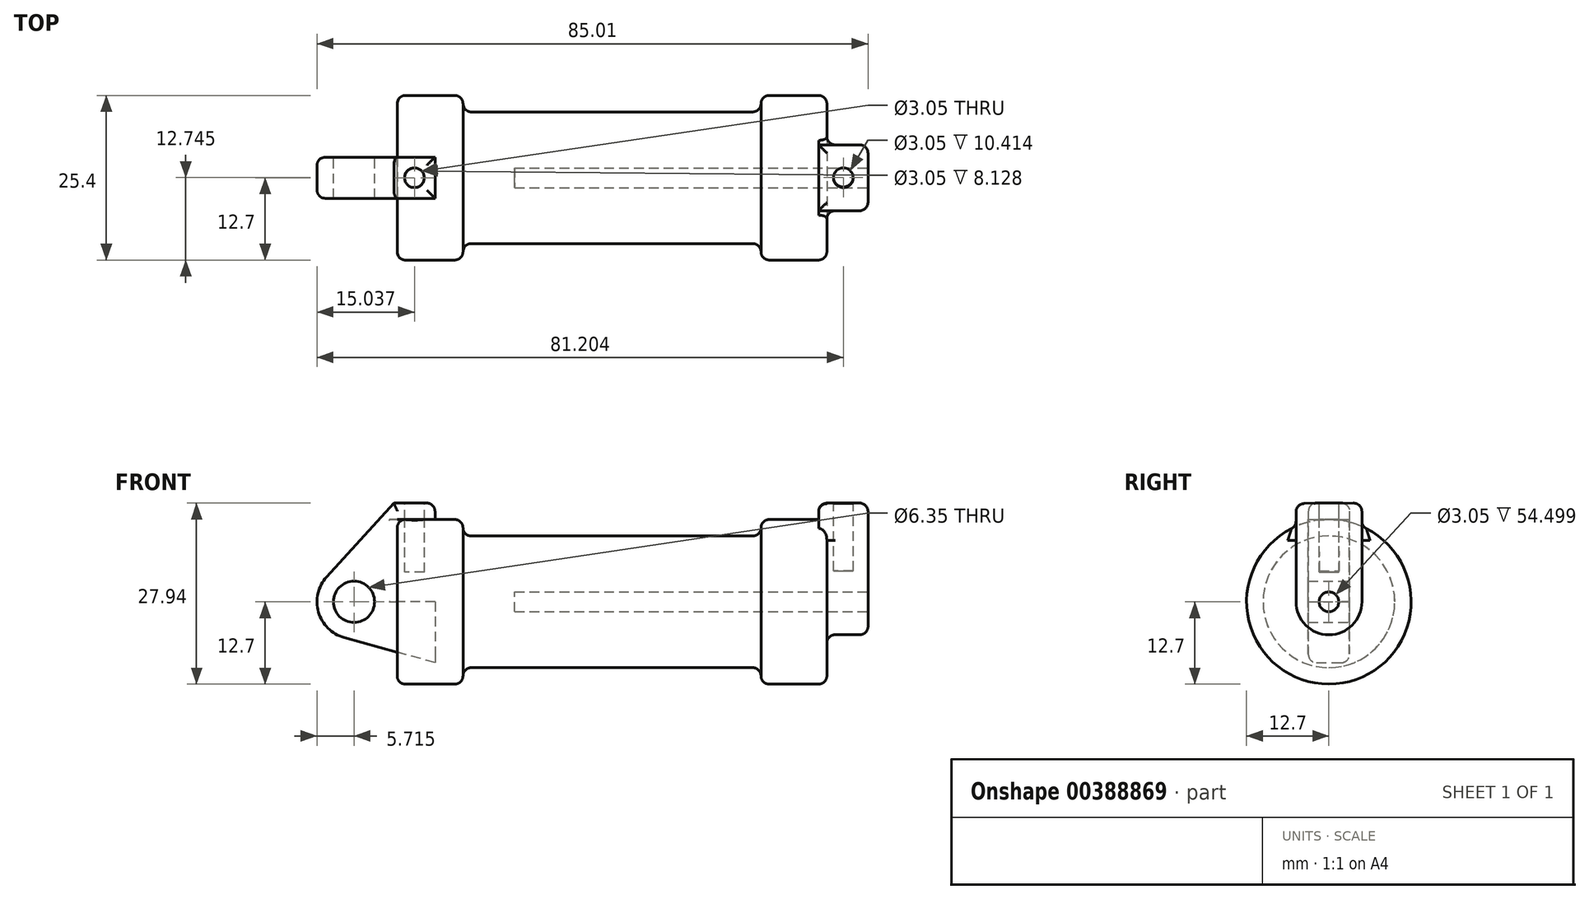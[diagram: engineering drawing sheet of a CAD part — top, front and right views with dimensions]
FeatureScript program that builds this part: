
annotation { "Feature Type Name" : "Feature", "Feature Type Description" : "" }
export const myFeature = defineFeature(function(context is Context, id is Id, definition is map)
    precondition{}
    {
        {
            var Q0;
            Q0=qCreatedBy(makeId("Front.planeOp"),FACE);
            var sketch = newSketch(context, id + "F0", { "sketchPlane" : qUnion([Q0])});
            skLineSegment(sketch, "E0", {"start": v(0, 0) * mm, "end": v(0, 12.7) * mm});
            skLineSegment(sketch, "E1", {"start": v(0, 12.7) * mm, "end": v(10.16, 12.7) * mm});
            skLineSegment(sketch, "E2", {"start": v(10.16, 12.7) * mm, "end": v(10.16, 10.16) * mm});
            skLineSegment(sketch, "E3", {"start": v(10.16, 10.16) * mm, "end": v(56.13, 10.16) * mm});
            skLineSegment(sketch, "E4", {"start": v(56.13, 10.16) * mm, "end": v(56.13, 12.7) * mm});
            skLineSegment(sketch, "E5", {"start": v(56.13, 12.7) * mm, "end": v(66.3, 12.7) * mm});
            skLineSegment(sketch, "E6", {"start": v(66.3, 12.7) * mm, "end": v(66.3, 0) * mm});
            skLineSegment(sketch, "E7", {"start": v(66.3, 0) * mm, "end": v(0, 0) * mm});
            skLineSegment(sketch, "E8", {"start": v(5.84, 15.24) * mm, "end": v(-0.5, 15.24) * mm});
            skLineSegment(sketch, "E9", {"start": v(-0.5, 15.24) * mm, "end": v(-10.88, 3.85) * mm});
            skLineSegment(sketch, "E10", {"start": v(0, 0) * mm, "end": v(-6.65, 0) * mm});
            skCircle(sketch, "E11", {"center": v(-6.65, 0) * mm, "radius": 5.72 * mm});
            skCircle(sketch, "E12", {"center": v(-6.65, 0) * mm, "radius": 3.18 * mm});
            skLineSegment(sketch, "E13", {"start": v(5.84, 15.24) * mm, "end": v(5.84, -9.4) * mm});
            skLineSegment(sketch, "E14", {"start": v(5.84, -9.4) * mm, "end": v(-8.18, -5.5) * mm});
            skSolve(sketch);
        }
        {
            var Q0;
            {var subQ0=sQuery(id+"F0.wireOp",EDGE,"E2");Q0=makeQuery(id+"F0.imprint","IMPRINT",FACE,{"disambiguationData":[TD([[makeQuery(id+"F0.imprint","IMPRINT",EDGE,{"derivedFrom":subQ0}),-1.0]])]});}
            var Q1;
            {var subQ0=sQuery(id+"F0.wireOp",EDGE,"E0");Q1=makeQuery(id+"F0.imprint","IMPRINT",FACE,{"disambiguationData":[TD([[makeQuery(id+"F0.imprint","IMPRINT",EDGE,{"derivedFrom":subQ0}),-1.0]])]});}
            var Q2;
            Q2=sQuery(id+"F0.wireOp",EDGE,"E7");
            revolve(context, id + "F1", {"entities" : qUnion([Q0, Q1]), "axis" : qUnion([Q2]), "revolveType" : RevolveType.FULL});
        }
        {
            var Q0;
            {var subQ5=sQuery(id+"F0.wireOp",EDGE,"E12");Q0=makeQuery(id+"F0.imprint","IMPRINT",FACE,{"disambiguationData":[TD([[makeQuery(id+"F0.imprint","IMPRINT",EDGE,{"derivedFrom":subQ5}),-1.0]])]});}
            var Q1;
            {var subQ0=sQuery(id+"F0.wireOp",EDGE,"E14");Q1=makeQuery(id+"F0.imprint","IMPRINT",FACE,{"disambiguationData":[TD([[makeQuery(id+"F0.imprint","IMPRINT",EDGE,{"derivedFrom":subQ0}),-1.0]])]});}
            var Q2;
            {var subQ1=sQuery(id+"F0.wireOp",EDGE,"E0");Q2=makeQuery(id+"F0.imprint","IMPRINT",FACE,{"disambiguationData":[TD([[makeQuery(id+"F0.imprint","IMPRINT",EDGE,{"derivedFrom":subQ1}),1.0]])]});}
            extrude(context, id + "F2", {"entities" : qUnion([Q0, Q1, Q2]), "endBound" : BoundingType.SYMMETRIC, "depth" : 6.35 * mm});
        }
        {
            var Q0;
            Q0=makeQuery(id+"F1.opRevolve","SWEPT_FACE",FACE,{"disambiguationData":[OSD([sQuery(id+"F0.wireOp",EDGE,"E6")])]});
            var sketch = newSketch(context, id + "F3", { "sketchPlane" : qUnion([Q0])});
            skCircle(sketch, "E15", {"center": v(0, 0) * mm, "radius": 1.52 * mm});
            skCircle(sketch, "E16", {"center": v(0, 0) * mm, "radius": 5.08 * mm});
            skLineSegment(sketch, "E17", {"start": v(5.08, 0) * mm, "end": v(5.08, 15.24) * mm});
            skLineSegment(sketch, "E18", {"start": v(-5.08, 0) * mm, "end": v(-5.08, 15.15) * mm});
            skLineSegment(sketch, "E19", {"start": v(-5.08, 15.15) * mm, "end": v(5.08, 15.24) * mm});
            skSolve(sketch);
        }
        {
            var Q0;
            {var subQ0=sQuery(id+"F3.wireOp",EDGE,"E17");var subQ1=sQuery(id+"F3.wireOp",EDGE,"E16");var subQ2=makeQuery(id+"F3.imprint","INTERSECT",VERTEX,{"derivedFrom":[subQ1,subQ0]});Q0=makeQuery(id+"F3.imprint","IMPRINT",FACE,{"disambiguationData":[TD([[makeQuery(id+"F3.imprint","IMPRINT",EDGE,{"disambiguationData":[TD([[subQ2,-1.0]])],"derivedFrom":subQ1}),-1.0]])]});}
            var Q1;
            Q1=makeQuery(id+"F3.imprint","IMPRINT",FACE,{"disambiguationData":[TD([[makeQuery(id+"F3.imprint","IMPRINT",EDGE,{"derivedFrom":sQuery(id+"F3.wireOp",EDGE,"E15")}),-1.0]])]});
            var Q2;
            {var subQ0=sQuery(id+"F3.wireOp",EDGE,"E19");Q2=makeQuery(id+"F3.imprint","IMPRINT",FACE,{"disambiguationData":[TD([[makeQuery(id+"F3.imprint","IMPRINT",EDGE,{"derivedFrom":subQ0}),-1.0]])]});}
            var Q3;
            Q3=makeQuery(id+"F3.imprint","IMPRINT",FACE,{"disambiguationData":[TD([[makeQuery(id+"F3.imprint","IMPRINT",EDGE,{"derivedFrom":sQuery(id+"F3.wireOp",EDGE,"E15")}),1.0]])]});
            extrude(context, id + "F4", {"entities" : qUnion([Q0, Q1, Q2, Q3]), "operationType" : NewBodyOperationType.ADD, "depth" : 6.35 * mm, "hasSecondDirection" : true, "secondDirectionOppositeDirection" : true, "secondDirectionDepth" : 1.27 * mm});
        }
        {
            var Q0;
            Q0=makeQuery(id+"F3.imprint","IMPRINT",FACE,{"disambiguationData":[TD([[makeQuery(id+"F3.imprint","IMPRINT",EDGE,{"derivedFrom":sQuery(id+"F3.wireOp",EDGE,"E15")}),1.0]])]});
            extrude(context, id + "F5", {"entities" : qUnion([Q0]), "operationType" : NewBodyOperationType.REMOVE, "oppositeDirection" : true, "depth" : 48.15 * mm, "hasSecondDirection" : true, "secondDirectionOppositeDirection" : false, "secondDirectionDepth" : 6.35 * mm});
        }
        {
            var Q0;
            Q0=makeQuery(id+"F4.opExtrude","SWEPT_FACE",FACE,{"disambiguationData":[OSD([sQuery(id+"F3.wireOp",EDGE,"E19")])]});
            var sketch = newSketch(context, id + "F6", { "sketchPlane" : qUnion([Q0])});
            skLineSegment(sketch, "E20", {"start": v(65.02, 0.13) * mm, "end": v(72.64, 0.13) * mm, "construction": true});
            skLineSegment(sketch, "E21", {"start": v(68.83, 5.21) * mm, "end": v(68.83, -4.95) * mm, "construction": true});
            skCircle(sketch, "E22", {"center": v(68.83, 0.13) * mm, "radius": 1.52 * mm});
            skSolve(sketch);
        }
        {
            var Q0;
            Q0=makeQuery(id+"F6.imprint","IMPRINT",FACE,{"disambiguationData":[TD([[makeQuery(id+"F6.imprint","IMPRINT",EDGE,{"derivedFrom":sQuery(id+"F6.wireOp",EDGE,"E22")}),1.0]])]});
            var Q1;
            Q1=sQuery(id+"F6.wireOp",EDGE,"E22");
            extrude(context, id + "F7", {"entities" : qUnion([Q0]), "operationType" : NewBodyOperationType.REMOVE, "surfaceEntities" : qUnion([Q1]), "oppositeDirection" : true, "depth" : 10.4 * mm});
        }
        {
            var Q0;
            Q0=makeQuery(id+"F2.opExtrude","SWEPT_FACE",FACE,{"disambiguationData":[OSD([sQuery(id+"F0.wireOp",EDGE,"E8")])]});
            var sketch = newSketch(context, id + "F8", { "sketchPlane" : qUnion([Q0])});
            skLineSegment(sketch, "E23.0", {"start": v(5.84, 3.18) * mm, "end": v(-0.5, 3.18) * mm});
            skLineSegment(sketch, "E23.1", {"start": v(5.84, -3.18) * mm, "end": v(5.84, 3.17) * mm});
            skLineSegment(sketch, "E23.2", {"start": v(5.84, -3.18) * mm, "end": v(-0.5, -3.18) * mm});
            skLineSegment(sketch, "E23.3", {"start": v(-0.5, -3.18) * mm, "end": v(-0.5, 3.17) * mm});
            skLineSegment(sketch, "E24", {"start": v(2.67, 3.18) * mm, "end": v(2.67, -3.18) * mm, "construction": true});
            skLineSegment(sketch, "E25", {"start": v(-0.5, 0) * mm, "end": v(5.84, 0) * mm, "construction": true});
            skCircle(sketch, "E26", {"center": v(2.67, 0) * mm, "radius": 1.52 * mm});
            skSolve(sketch);
        }
        {
            var Q0;
            Q0=makeQuery(id+"F8.imprint","IMPRINT",FACE,{"disambiguationData":[TD([[makeQuery(id+"F8.imprint","IMPRINT",EDGE,{"derivedFrom":sQuery(id+"F8.wireOp",EDGE,"E26")}),1.0]])]});
            var Q1;
            Q1=sQuery(id+"F8.wireOp",EDGE,"E26");
            extrude(context, id + "F9", {"entities" : qUnion([Q0]), "operationType" : NewBodyOperationType.REMOVE, "surfaceEntities" : qUnion([Q1]), "oppositeDirection" : true, "depth" : 10.67 * mm});
        }
        {
            var Q0;
            Q0=makeQuery(id+"F1.opRevolve","SWEPT_EDGE",EDGE,{"disambiguationData":[OSD([sQuery(id+"F0.wireOp",EDGE,"E0"),sQuery(id+"F0.wireOp",EDGE,"E1")])]});
            var Q1;
            Q1=makeQuery(id+"F1.opRevolve","SWEPT_EDGE",EDGE,{"disambiguationData":[OSD([sQuery(id+"F0.wireOp",EDGE,"E1"),sQuery(id+"F0.wireOp",EDGE,"E2")])]});
            var Q2;
            Q2=makeQuery(id+"F1.opRevolve","SWEPT_EDGE",EDGE,{"disambiguationData":[OSD([sQuery(id+"F0.wireOp",EDGE,"E4"),sQuery(id+"F0.wireOp",EDGE,"E5")])]});
            var Q3;
            Q3=makeQuery(id+"F1.opRevolve","SWEPT_EDGE",EDGE,{"disambiguationData":[OSD([sQuery(id+"F0.wireOp",EDGE,"E5"),sQuery(id+"F0.wireOp",EDGE,"E6")])]});
            var Q4;
            Q4=makeQuery(id+"F1.opRevolve","SWEPT_EDGE",EDGE,{"disambiguationData":[OSD([sQuery(id+"F0.wireOp",EDGE,"E2"),sQuery(id+"F0.wireOp",EDGE,"E3")])]});
            var Q5;
            Q5=makeQuery(id+"F1.opRevolve","SWEPT_EDGE",EDGE,{"disambiguationData":[OSD([sQuery(id+"F0.wireOp",EDGE,"E3"),sQuery(id+"F0.wireOp",EDGE,"E4")])]});
            fillet(context, id + "F10", {"entities" : qUnion([Q0, Q1, Q2, Q3, Q4, Q5]), "radius" : 1.27 * mm, "tangentPropagation" : true, "allowEdgeOverflow" : false});
        }
        {
            var Q0;
            Q0=makeQuery(id+"F2.opExtrude","CAP_EDGE",EDGE,{"disambiguationData":[OSD([sQuery(id+"F0.wireOp",EDGE,"E9")])],"isStart":true});
            var Q1;
            Q1=makeQuery(id+"F2.opExtrude","CAP_EDGE",EDGE,{"disambiguationData":[OSD([sQuery(id+"F0.wireOp",EDGE,"E8")])],"isStart":true});
            var Q2;
            Q2=makeQuery(id+"F2.opExtrude","SWEPT_EDGE",EDGE,{"disambiguationData":[OSD([sQuery(id+"F0.wireOp",EDGE,"E8"),sQuery(id+"F0.wireOp",EDGE,"E13")])]});
            var Q3;
            Q3=makeQuery(id+"F2.opExtrude","CAP_EDGE",EDGE,{"disambiguationData":[OSD([sQuery(id+"F0.wireOp",EDGE,"E8")])],"isStart":false});
            var Q4;
            Q4=makeQuery(id+"F2.opExtrude","CAP_EDGE",EDGE,{"disambiguationData":[OSD([sQuery(id+"F0.wireOp",EDGE,"E9")])],"isStart":false});
            var Q5;
            Q5=makeQuery(id+"F2.opExtrude","CAP_EDGE",EDGE,{"disambiguationData":[OSD([sQuery(id+"F0.wireOp",EDGE,"E11")])],"isStart":true});
            var Q6;
            Q6=makeQuery(id+"F2.opExtrude","CAP_EDGE",EDGE,{"disambiguationData":[OSD([sQuery(id+"F0.wireOp",EDGE,"E14")])],"isStart":true});
            var Q7;
            Q7=makeQuery(id+"F2.opExtrude","CAP_EDGE",EDGE,{"disambiguationData":[OSD([sQuery(id+"F0.wireOp",EDGE,"E11")])],"isStart":false});
            var Q8;
            Q8=makeQuery(id+"F2.opExtrude","CAP_EDGE",EDGE,{"disambiguationData":[OSD([sQuery(id+"F0.wireOp",EDGE,"E14")])],"isStart":false});
            var Q9;
            Q9=makeQuery(id+"F2.opExtrude","CAP_EDGE",EDGE,{"disambiguationData":[OSD([sQuery(id+"F0.wireOp",EDGE,"E0")])],"isStart":true});
            fillet(context, id + "F11", {"entities" : qUnion([Q0, Q1, Q2, Q3, Q4, Q5, Q6, Q7, Q8, Q9]), "radius" : 1.27 * mm, "tangentPropagation" : true, "allowEdgeOverflow" : false});
        }
        {
            var Q0;
            Q0=makeQuery(id+"F4.opExtrude","CAP_EDGE",EDGE,{"disambiguationData":[OSD([sQuery(id+"F3.wireOp",EDGE,"E17")])],"isStart":false});
            var Q1;
            Q1=makeQuery(id+"F4.opExtrude","CAP_EDGE",EDGE,{"disambiguationData":[OSD([sQuery(id+"F3.wireOp",EDGE,"E16")])],"isStart":false});
            var Q2;
            Q2=makeQuery(id+"F4.opExtrude","SWEPT_EDGE",EDGE,{"disambiguationData":[OSD([sQuery(id+"F3.wireOp",EDGE,"E18"),sQuery(id+"F3.wireOp",EDGE,"E19")])]});
            var Q3;
            Q3=makeQuery(id+"F4.opExtrude","CAP_EDGE",EDGE,{"disambiguationData":[OSD([sQuery(id+"F3.wireOp",EDGE,"E19")])],"isStart":false});
            var Q4;
            Q4=makeQuery(id+"F4.opExtrude","SWEPT_EDGE",EDGE,{"disambiguationData":[OSD([sQuery(id+"F3.wireOp",EDGE,"E17"),sQuery(id+"F3.wireOp",EDGE,"E19")])]});
            var Q5;
            Q5=makeQuery(id+"F4.opExtrude","CAP_EDGE",EDGE,{"disambiguationData":[OSD([sQuery(id+"F3.wireOp",EDGE,"E19")])],"isStart":true});
            var Q6;
            Q6=makeQuery(id+"F4.boolean.opBoolean","INTERSECT",EDGE,{"derivedFrom":[makeQuery(id+"F1.opRevolve","SWEPT_FACE",FACE,{"disambiguationData":[OSD([sQuery(id+"F0.wireOp",EDGE,"E6")])]}),makeQuery(id+"F4.opExtrude","SWEPT_FACE",FACE,{"disambiguationData":[OSD([sQuery(id+"F3.wireOp",EDGE,"E18")])]})]});
            fillet(context, id + "F12", {"entities" : qUnion([Q0, Q1, Q2, Q3, Q4, Q5, Q6]), "radius" : 1.27 * mm, "tangentPropagation" : true, "allowEdgeOverflow" : false});
        }
    });
